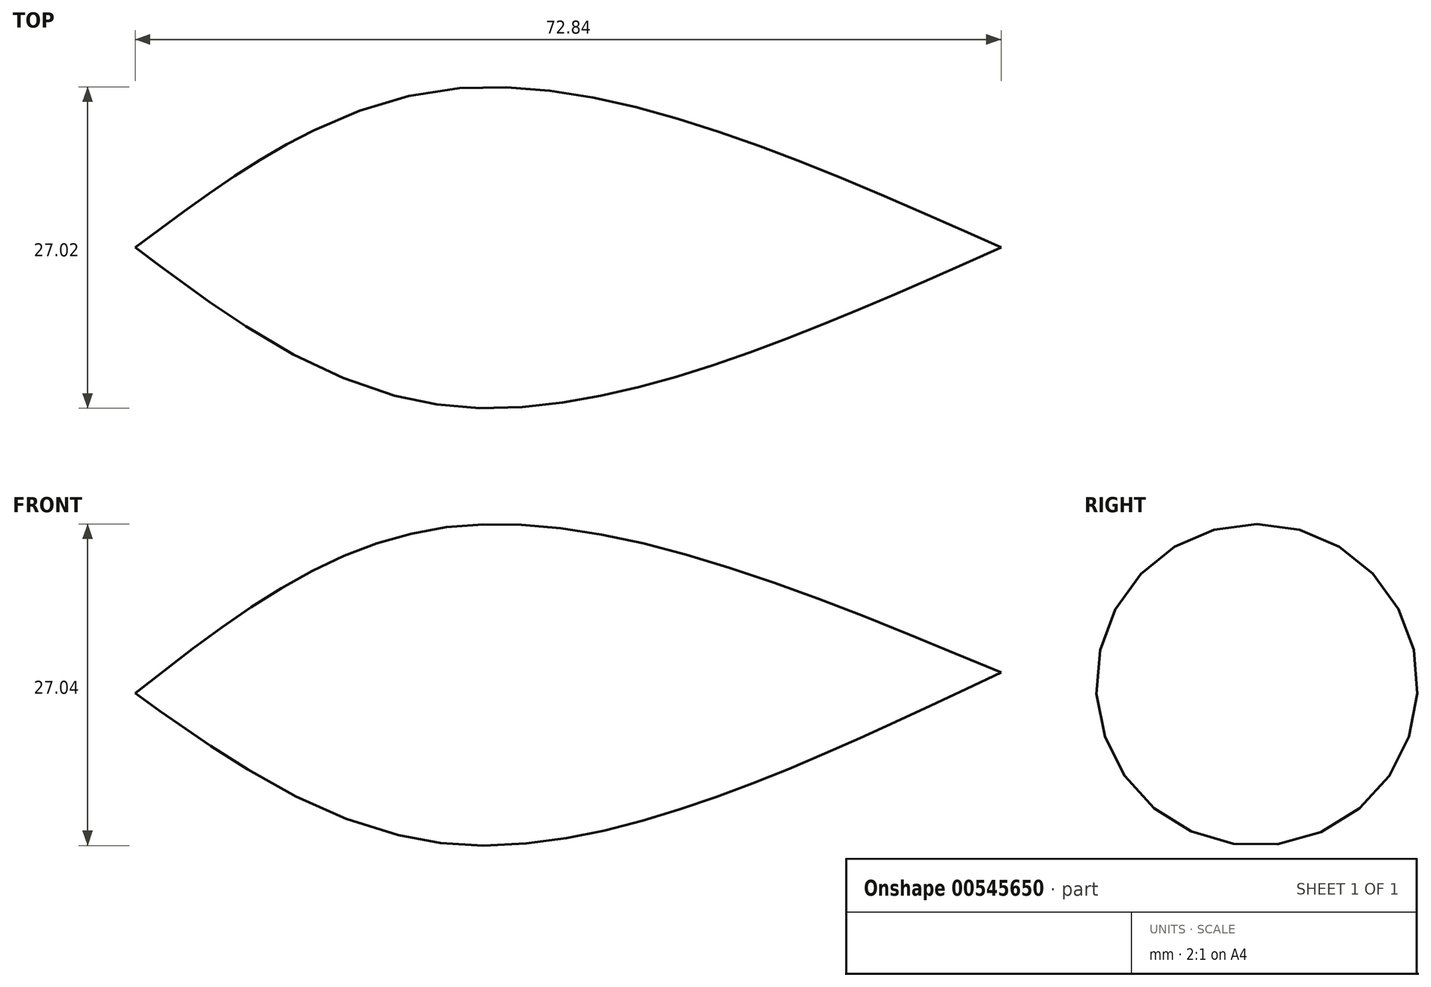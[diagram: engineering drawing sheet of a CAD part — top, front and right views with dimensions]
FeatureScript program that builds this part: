
annotation { "Feature Type Name" : "Feature", "Feature Type Description" : "" }
export const myFeature = defineFeature(function(context is Context, id is Id, definition is map)
    precondition{}
    {
        {
            var Q0;
            Q0=qCreatedBy(makeId("Front.planeOp"),FACE);
            var sketch = newSketch(context, id + "F0", { "sketchPlane" : qUnion([Q0])});
            skFitSpline(sketch, "E0", {"points": [v(-55.29, 10.97) * mm, v(-28.52, 25.01) * mm, v(17.55, 12.73) * mm], "startDerivative": vector(55.43, 43.59) * mm, "endDerivative": vector(88.98, -37.03) * mm});
            skFitSpline(sketch, "E1", {"points": [v(17.55, 12.73) * mm, v(17.55, 59.24) * mm], "startDerivative": vector(0, 46.51) * mm, "endDerivative": vector(0, 46.51) * mm});
            skLineSegment(sketch, "E2", {"start": v(-55.29, 10.97) * mm, "end": v(17.55, 12.73) * mm});
            skSolve(sketch);
        }
        {
            var Q0;
            Q0 = qSketchRegion(id + "F0", true);
            var Q1;
            Q1=sQuery(id+"F0.wireOp",EDGE,"E2");
            revolve(context, id + "F1", {"entities" : qUnion([Q0]), "axis" : qUnion([Q1]), "revolveType" : RevolveType.FULL});
        }
    });
